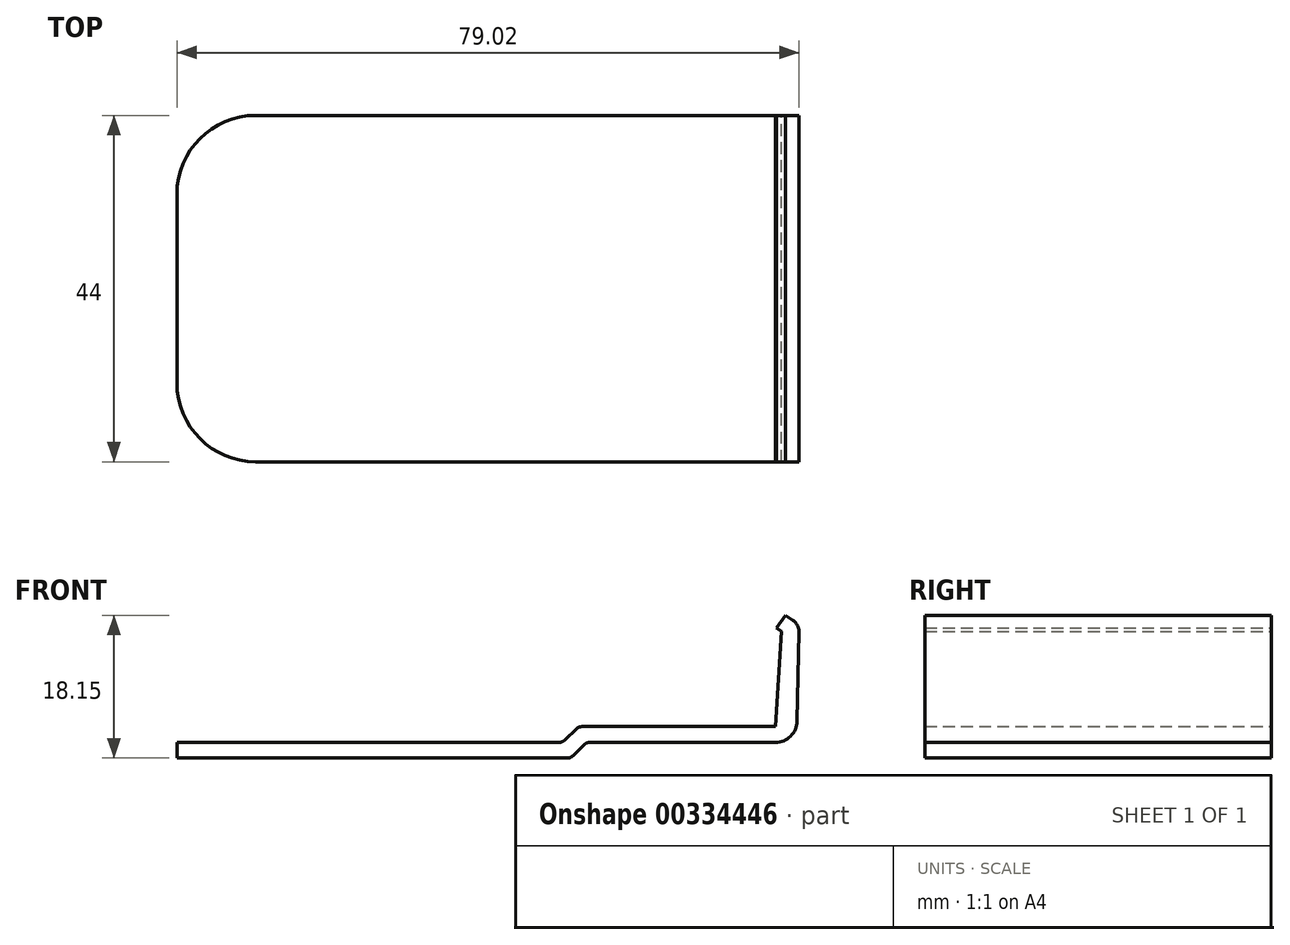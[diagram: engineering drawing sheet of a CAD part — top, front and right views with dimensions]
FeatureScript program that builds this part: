
annotation { "Feature Type Name" : "Feature", "Feature Type Description" : "" }
export const myFeature = defineFeature(function(context is Context, id is Id, definition is map)
    precondition{}
    {
        {
            var Q0;
            Q0=qCreatedBy(makeId("Front.planeOp"),FACE);
            var sketch = newSketch(context, id + "F0", { "sketchPlane" : qUnion([Q0])});
            skLineSegment(sketch, "E0", {"start": v(-0.4, 0) * mm, "end": v(-40, 0) * mm});
            skLineSegment(sketch, "E1", {"start": v(-40, 0) * mm, "end": v(-40, 2) * mm});
            skLineSegment(sketch, "E2", {"start": v(-40, 2) * mm, "end": v(-1.43, 2) * mm});
            skLineSegment(sketch, "E3", {"start": v(-0.73, 2.28) * mm, "end": v(0.75, 3.72) * mm});
            skLineSegment(sketch, "E4", {"start": v(1.44, 4) * mm, "end": v(26.04, 4) * mm});
            skLineSegment(sketch, "E5", {"start": v(0.3, 0.28) * mm, "end": v(1.77, 1.72) * mm});
            skLineSegment(sketch, "E6", {"start": v(2.46, 2) * mm, "end": v(26.04, 2) * mm});
            skPoint(sketch, "E7.visualSharp", {"position": v(-1.02, 2) * mm});
            skArc(sketch, "E7.filletArc", {"start": v(-1.43, 2) * mm, "mid": v(-1.05, 2.07) * mm, "end": v(-0.73, 2.28) * mm});
            skPoint(sketch, "E8.visualSharp", {"position": v(0, 0) * mm});
            skArc(sketch, "E8.filletArc", {"start": v(-0.4, 0) * mm, "mid": v(-0.03, 0.07) * mm, "end": v(0.3, 0.28) * mm});
            skPoint(sketch, "E9.visualSharp", {"position": v(2.06, 2) * mm});
            skArc(sketch, "E9.filletArc", {"start": v(2.46, 2) * mm, "mid": v(2.09, 1.93) * mm, "end": v(1.77, 1.72) * mm});
            skPoint(sketch, "E10.visualSharp", {"position": v(1.04, 4) * mm});
            skArc(sketch, "E10.filletArc", {"start": v(1.44, 4) * mm, "mid": v(1.07, 3.93) * mm, "end": v(0.75, 3.72) * mm});
            skLineSegment(sketch, "E11", {"start": v(26.04, 4) * mm, "end": v(26.83, 16.07) * mm});
            skLineSegment(sketch, "E12", {"start": v(26.83, 16.07) * mm, "end": v(26.19, 16.51) * mm});
            skLineSegment(sketch, "E13", {"start": v(26.19, 16.51) * mm, "end": v(27.33, 18.15) * mm});
            skLineSegment(sketch, "E14", {"start": v(27.33, 18.15) * mm, "end": v(28.27, 17.5) * mm});
            skArc(sketch, "E15", {"start": v(29.02, 16.03) * mm, "mid": v(28.83, 16.85) * mm, "end": v(28.27, 17.5) * mm});
            skLineSegment(sketch, "E16", {"start": v(29.02, 16.03) * mm, "end": v(28.8, 4.7) * mm});
            skArc(sketch, "E17", {"start": v(26.04, 2) * mm, "mid": v(27.97, 2.79) * mm, "end": v(28.8, 4.7) * mm});
            skSolve(sketch);
        }
        {
            var Q0;
            Q0=makeQuery(id+"F0.imprint","IMPRINT",FACE,{"disambiguationData":[TD([[makeQuery(id+"F0.imprint","IMPRINT",EDGE,{"derivedFrom":sQuery(id+"F0.wireOp",EDGE,"E0")}),-1.0]])]});
            extrude(context, id + "F1", {"entities" : qUnion([Q0]), "depth" : 44 * mm, "symmetric" : true});
        }
        {
            var Q0;
            Q0=makeQuery(id+"F1.opExtrude","SWEPT_FACE",FACE,{"disambiguationData":[OSD([sQuery(id+"F0.wireOp",EDGE,"E2")])]});
            var sketch = newSketch(context, id + "F2", { "sketchPlane" : qUnion([Q0])});
            skLineSegment(sketch, "E18", {"start": v(-50, -12) * mm, "end": v(-50, 12) * mm});
            skArc(sketch, "E19", {"start": v(-50, -12) * mm, "mid": v(-47.07, -19.07) * mm, "end": v(-40, -22) * mm});
            skArc(sketch, "E20", {"start": v(-50, 12) * mm, "mid": v(-47.07, 19.07) * mm, "end": v(-40, 22) * mm});
            skSolve(sketch);
        }
        {
            var Q0;
            Q0=makeQuery(id+"F2.imprint","IMPRINT",FACE,{"disambiguationData":[TD([[makeQuery(id+"F2.imprint","IMPRINT",EDGE,{"derivedFrom":sQuery(id+"F2.wireOp",EDGE,"E18")}),-1.0]])]});
            extrude(context, id + "F3", {"entities" : qUnion([Q0]), "operationType" : NewBodyOperationType.ADD, "oppositeDirection" : true, "depth" : 2 * mm});
        }
    });
